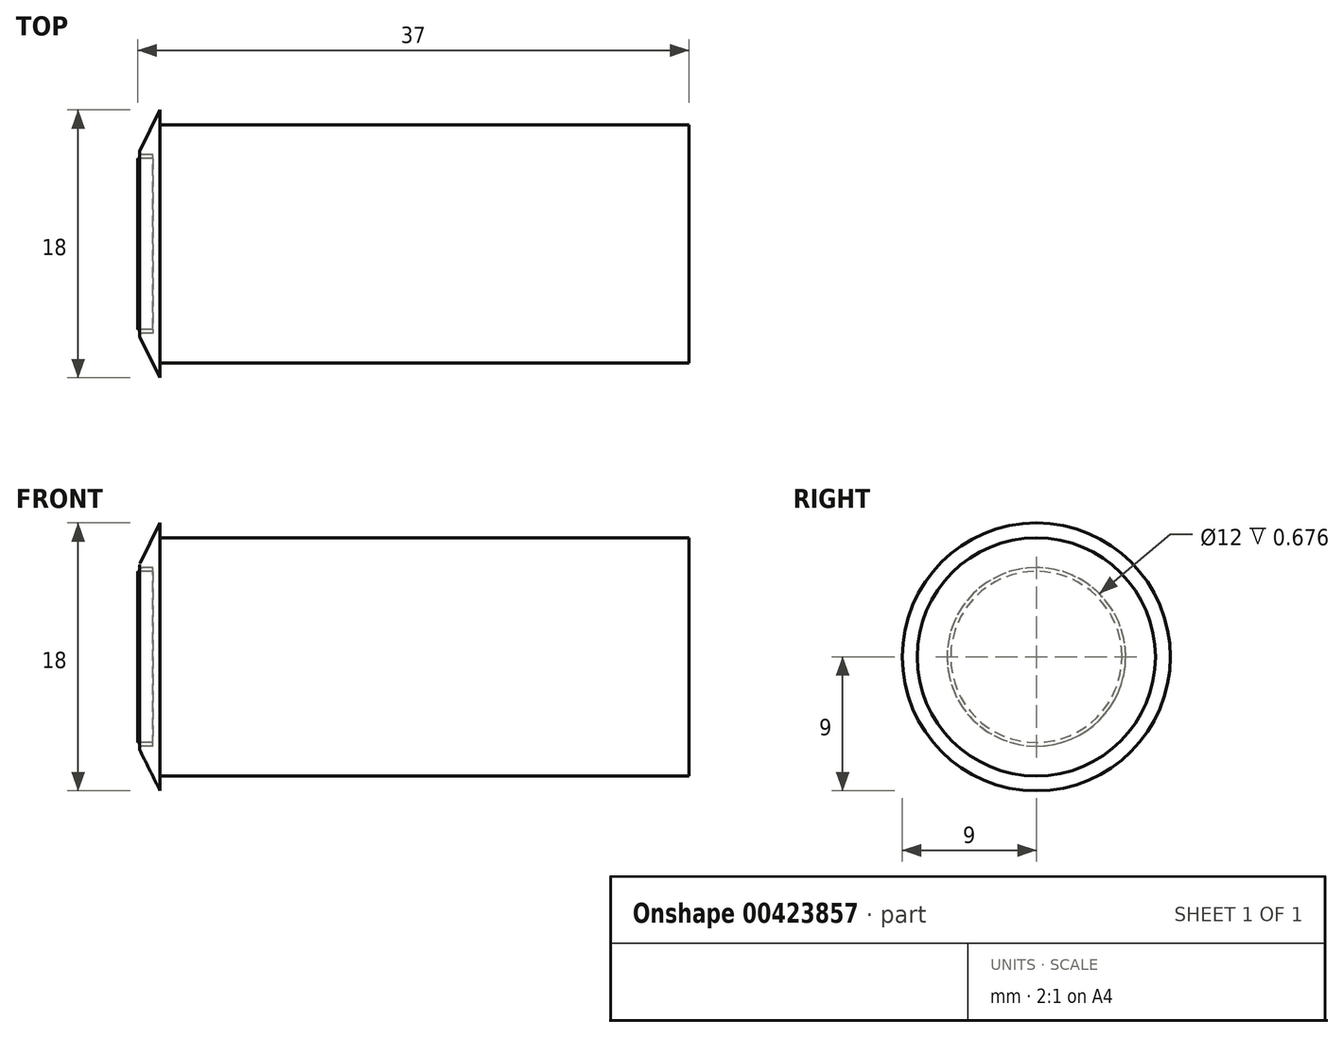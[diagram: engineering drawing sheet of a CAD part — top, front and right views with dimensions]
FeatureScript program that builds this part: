
annotation { "Feature Type Name" : "Feature", "Feature Type Description" : "" }
export const myFeature = defineFeature(function(context is Context, id is Id, definition is map)
    precondition{}
    {
        {
            var Q0;
            Q0=qCreatedBy(makeId("Front.planeOp"),FACE);
            var sketch = newSketch(context, id + "F0", { "sketchPlane" : qUnion([Q0])});
            skLineSegment(sketch, "E0", {"start": v(0, 0) * mm, "end": v(0, 6) * mm});
            skLineSegment(sketch, "E1", {"start": v(0, 6) * mm, "end": v(1.5, 9) * mm});
            skLineSegment(sketch, "E2", {"start": v(1.5, 9) * mm, "end": v(1.5, 8) * mm});
            skLineSegment(sketch, "E3", {"start": v(1.5, 8) * mm, "end": v(37, 8) * mm});
            skLineSegment(sketch, "E4", {"start": v(37, 8) * mm, "end": v(37, 0) * mm});
            skLineSegment(sketch, "E5", {"start": v(37, 0) * mm, "end": v(0, 0) * mm});
            skSolve(sketch);
        }
        {
            var Q0;
            Q0=qSketchRegion(id+"F0",true);
            var Q1;
            Q1=sQuery(id+"F0.wireOp",EDGE,"E5");
            revolve(context, id + "F1", {"entities" : qUnion([Q0]), "axis" : qUnion([Q1]), "revolveType" : RevolveType.FULL});
        }
        {
            var Q0;
            Q0=makeQuery(id+"F1.opRevolve","SWEPT_FACE",FACE,{"disambiguationData":[OSD([sQuery(id+"F0.wireOp",EDGE,"E0")])]});
            var sketch = newSketch(context, id + "F2", { "sketchPlane" : qUnion([Q0])});
            skCircle(sketch, "E6", {"center": v(0, 0) * mm, "radius": 5.75 * mm});
            skCircle(sketch, "E7", {"center": v(0, 0) * mm, "radius": 6 * mm});
            skSolve(sketch);
        }
        {
            var Q0;
            Q0=qSketchRegion(id+"F2",true);
            extrude(context, id + "F3", {"entities" : qUnion([Q0]), "operationType" : NewBodyOperationType.REMOVE, "oppositeDirection" : true, "depth" : 1 * mm});
        }
        {
            var Q0;
            Q0=makeQuery(id+"F3.boolean.opBoolean","MERGE",EDGE,{"derivedFrom":[makeQuery(id+"F1.opRevolve","SWEPT_EDGE",EDGE,{"disambiguationData":[OSD([sQuery(id+"F0.wireOp",EDGE,"E0"),sQuery(id+"F0.wireOp",EDGE,"E1")])]}),makeQuery(id+"F3.opExtrude","CAP_EDGE",EDGE,{"disambiguationData":[OSD([sQuery(id+"F2.wireOp",EDGE,"E7")])],"isStart":true})]});
            var Q1;
            Q1=makeQuery(id+"F3.boolean.opBoolean","COPY",EDGE,{"derivedFrom":makeQuery(id+"F3.opExtrude","CAP_EDGE",EDGE,{"disambiguationData":[OSD([sQuery(id+"F2.wireOp",EDGE,"E6")])],"isStart":true})});
            fillet(context, id + "F4", {"entities" : qUnion([Q0, Q1]), "radius" : 0.2 * mm, "tangentPropagation" : true, "allowEdgeOverflow" : false});
        }
    });
